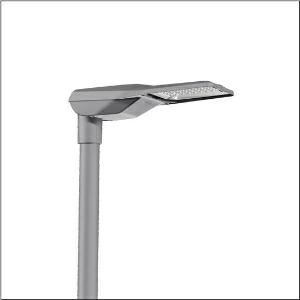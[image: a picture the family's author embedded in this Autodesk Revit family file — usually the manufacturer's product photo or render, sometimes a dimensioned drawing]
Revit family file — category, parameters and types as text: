
# Revit family: streetlight_sl_21_iq_mini___st0_5a_5xe2b31d08hb_2e1a
name_source: partatom
category: Lighting Fixtures
units: mm (PartAtom-declared; Revit-internal decimal feet)

## family parameters
Cut with Voids When Loaded = No
Host = Face
Light Source = No
Part Type = Normal
Room Calculation Point = No
Round Connector Dimension = Use Diameter
Shared = No

## types (1)
- --- (1 x LED, 9450 lm, 70.9 W, 3000K)
    Apparent Load = 71 VA
    CIE Flux Codes = 41 75 97 100 100
    Color Rendering = 70
    Color Temperature = 3000K
    Default Elevation = 1800 mm
    Description = Streetlight SL 21 iQ mini, mast luminaire, primary light control with lens, of PMMA, primary optical cover: cover, of toughened safety glass, transparent, light distribution: ST0.5a, light emission: direct distribution, primary light characteristic: asymmetric, installation type: post-top, side-entry, LED, High Power LED, rated luminous flux: 9.450lm, luminous efficacy: 133lm/W, light colour: 730, colour temperature: 3000K, control: Auto-Match, Temp-Guard, Lumen-Switch, Night-Set, Smart-Wire, Light-Fading, Desk-Remote (wireless, voltage-free reading and setting of iQ features in the workshop via application-optimized NFC function/RFID function), optimised constant luminous flux control (CLO 2.0), presetting dimming linear, mains connection: 220..240V, AC, 50/60Hz, start of lifetime: 71W, end of service life: 75W, reduction: 31W, luminaire housing, of diecast aluminium, powder-coated, Siteco® metallic grey (DB 702S), corrosivity category C5 mid according to DIN EN ISO 12944, please order mast flange separately, inclination adjustable: 0°, 5°, 10°, 15°, sealing non-destructively replaceable, multi-level sealing system, length: 628mm, width: 235mm, height: 110mm, mast flange for spigot size: 42mm (side-entry): 5XC10008XM4, 60/48mm (side-entry/post-top): 5XC10108XM2, 76/60mm (side-entry/post-top): 5XC10108XM1, protection rating (complete): IP66, insulation class (complete): insulation class II (safety insulation), certification: CE, ENEC, ENEC+, VDE, impact resistance: IK09, permissible operating ambient temperature for outdoor applications: -40..+50°C, standard-compliant lighting for roads and squares, packaging unit: 1 piece

Light Distribution: ST0.5a
    Height = 110 mm
    Lamp = 1 x LED
    Lamp Light Flux = 9450 lm
    Lamp Power = 70.9 W
    Lamp count = 1
    Length = 625 mm
    Luminous efficacy = 133 lm/W
    Manufacturer = Siteco
    ModVariant = No
    Model = 5XE2B31D08HB
    Number of Poles = 1
    OnlyDefault = Yes
    Power Factor = 1
    Product Name = Streetlight SL 21 iQ mini | ST0.5a
    Product group = mast luminaire | pylon top
    ProductGroupID = 6100
    Protection Class = Protection class II
    Protection Degree = IP 66
    RLX_Detail_Level = 1
    RLX_Emergency_Light_Flux = 0 lm
    RLX_Emergency_Type = 0
    RLX_Emergency_Type_DB = No
    RlxData = <blob elided: 103637 chars, md5=67028424>
    Socket = socket
    Standby Power = 0 W
    System Light Flux = 9450 lm
    System Power = 71 W
    Type Comments = factory setting: luminous flux: 100 % | dim-lin: 254 | 711 mA
    Type Image = l_1003519.jpg
    URL = http://relux.com
    VarID = @adj_090951
    Voltage = 0 V
    Weight = 0.00 kg
    Width = 234 mm

## geometry (parser evidence)
native form markers: Blend x4, Sweep x11
no freeform markers — native parametric forms only
